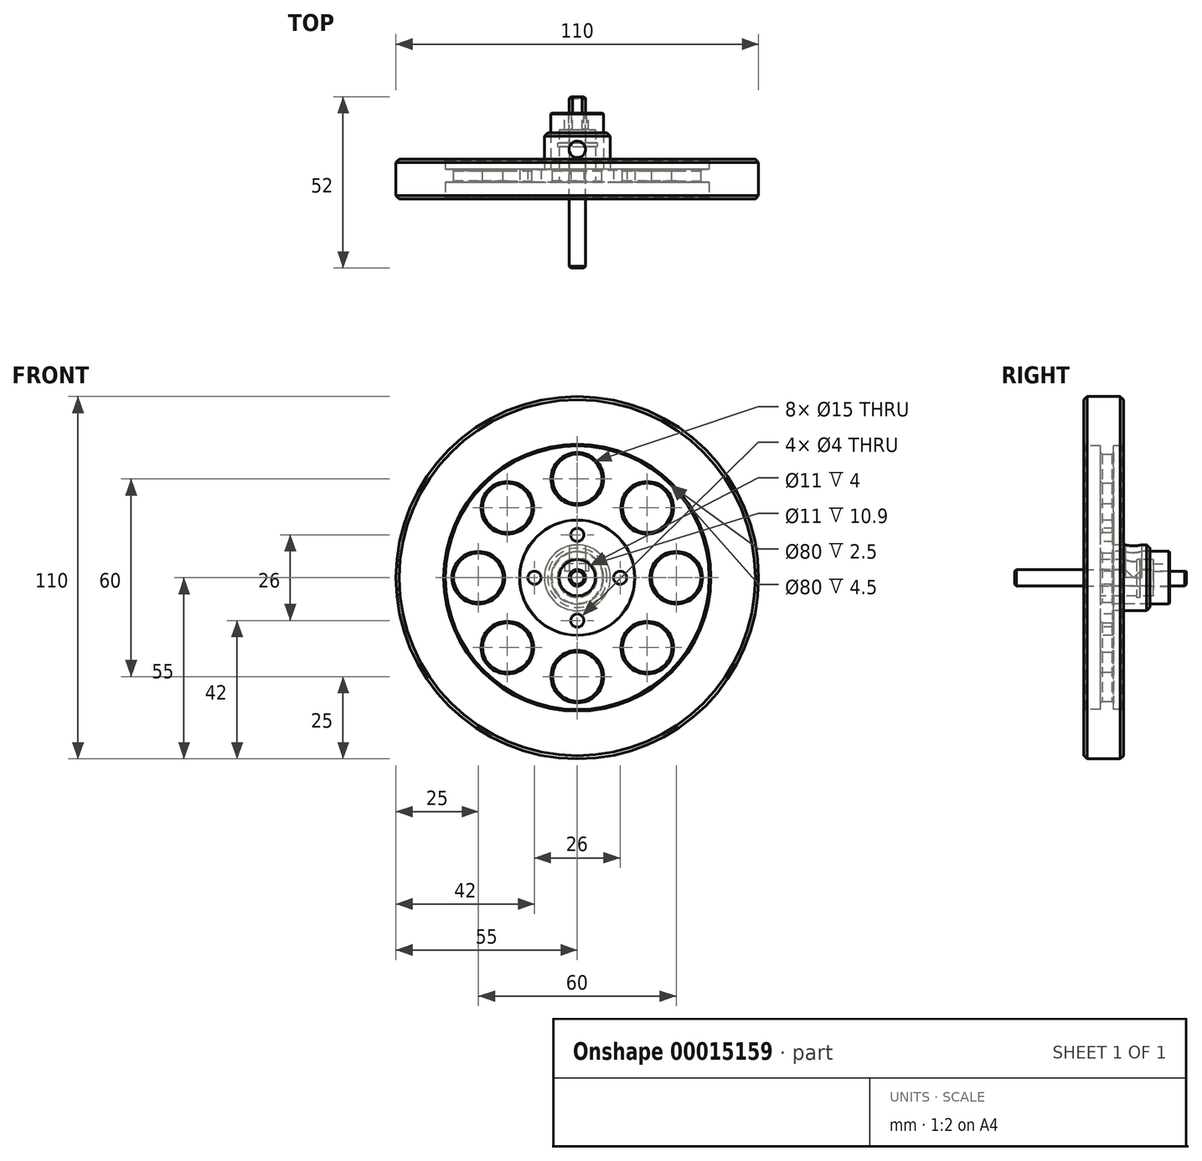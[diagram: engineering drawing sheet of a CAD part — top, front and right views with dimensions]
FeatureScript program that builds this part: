
annotation { "Feature Type Name" : "Feature", "Feature Type Description" : "" }
export const myFeature = defineFeature(function(context is Context, id is Id, definition is map)
    precondition{}
    {
        {
            var Q0;
            Q0=qCreatedBy(makeId("Right.planeOp"),FACE);
            var sketch = newSketch(context, id + "F0", { "sketchPlane" : qUnion([Q0])});
            skLineSegment(sketch, "E0", {"start": v(0, 5.5) * mm, "end": v(0, 17.5) * mm});
            skLineSegment(sketch, "E1", {"start": v(0, 17.5) * mm, "end": v(4, 17.5) * mm});
            skLineSegment(sketch, "E2", {"start": v(4, 17.5) * mm, "end": v(4, 8) * mm});
            skLineSegment(sketch, "E3", {"start": v(4, 8) * mm, "end": v(21, 8) * mm});
            skLineSegment(sketch, "E4", {"start": v(21, 8) * mm, "end": v(21, 2.75) * mm});
            skLineSegment(sketch, "E5", {"start": v(16, 2.75) * mm, "end": v(16, 5.5) * mm});
            skLineSegment(sketch, "E6", {"start": v(12, 5.5) * mm, "end": v(12, 6) * mm});
            skLineSegment(sketch, "E7", {"start": v(12, 6) * mm, "end": v(10.9, 6) * mm});
            skLineSegment(sketch, "E8", {"start": v(10.9, 6) * mm, "end": v(10.9, 5.5) * mm});
            skLineSegment(sketch, "E9", {"start": v(10.9, 5.5) * mm, "end": v(0, 5.5) * mm});
            skLineSegment(sketch, "E10", {"start": v(16, 2.75) * mm, "end": v(21, 2.75) * mm});
            skPoint(sketch, "E11.end.orphan", {"position": v(16, 0) * mm});
            skPoint(sketch, "E11.start.orphan", {"position": v(21, 0) * mm});
            skLineSegment(sketch, "E12", {"start": v(0, 0) * mm, "end": v(21, 0) * mm, "construction": true});
            skLineSegment(sketch, "E13", {"start": v(12, 5.5) * mm, "end": v(16, 5.5) * mm});
            skSolve(sketch);
        }
        {
            var Q0;
            Q0=makeQuery(id+"F0.imprint","IMPRINT",FACE,{"disambiguationData":[TD([[makeQuery(id+"F0.imprint","IMPRINT",EDGE,{"derivedFrom":sQuery(id+"F0.wireOp",EDGE,"E0")}),-1.0]])]});
            var Q1;
            Q1=sQuery(id+"F0.wireOp",EDGE,"E12");
            revolve(context, id + "F1", {"entities" : qUnion([Q0]), "axis" : qUnion([Q1]), "revolveType" : RevolveType.FULL});
        }
        {
            var Q0;
            Q0=makeQuery(id+"F1.opRevolve","SWEPT_FACE",FACE,{"disambiguationData":[OSD([sQuery(id+"F0.wireOp",EDGE,"E0")])]});
            var sketch = newSketch(context, id + "F2", { "sketchPlane" : qUnion([Q0])});
            skCircle(sketch, "E14", {"center": v(0, 0) * mm, "radius": 13 * mm, "construction": true});
            skLineSegment(sketch, "E15", {"start": v(0, 0) * mm, "end": v(-17.5, 0) * mm, "construction": true});
            skCircle(sketch, "E16", {"center": v(-13, 0) * mm, "radius": 2 * mm});
            skCircle(sketch, "E17.1.0", {"center": v(0, -13) * mm, "radius": 2 * mm});
            skCircle(sketch, "E17.2.0", {"center": v(13, 0) * mm, "radius": 2 * mm});
            skCircle(sketch, "E17.3.0", {"center": v(0, 13) * mm, "radius": 2 * mm});
            skSolve(sketch);
        }
        {
            var Q0;
            Q0=makeQuery(id+"F2.imprint","IMPRINT",FACE,{"disambiguationData":[TD([[makeQuery(id+"F2.imprint","IMPRINT",EDGE,{"derivedFrom":sQuery(id+"F2.wireOp",EDGE,"E17.3.0")}),1.0]])]});
            var Q1;
            Q1=makeQuery(id+"F2.imprint","IMPRINT",FACE,{"disambiguationData":[TD([[makeQuery(id+"F2.imprint","IMPRINT",EDGE,{"derivedFrom":sQuery(id+"F2.wireOp",EDGE,"E16")}),1.0]])]});
            var Q2;
            Q2=makeQuery(id+"F2.imprint","IMPRINT",FACE,{"disambiguationData":[TD([[makeQuery(id+"F2.imprint","IMPRINT",EDGE,{"derivedFrom":sQuery(id+"F2.wireOp",EDGE,"E17.1.0")}),1.0]])]});
            var Q3;
            Q3=makeQuery(id+"F2.imprint","IMPRINT",FACE,{"disambiguationData":[TD([[makeQuery(id+"F2.imprint","IMPRINT",EDGE,{"derivedFrom":sQuery(id+"F2.wireOp",EDGE,"E17.2.0")}),1.0]])]});
            extrude(context, id + "F3", {"entities" : qUnion([Q0, Q1, Q2, Q3]), "operationType" : NewBodyOperationType.REMOVE, "endBound" : BoundingType.THROUGH_ALL, "oppositeDirection" : true, "depth" : 25 * mm});
        }
        {
            var Q0;
            Q0=makeQuery(id+"F1.opRevolve","SWEPT_EDGE",EDGE,{"disambiguationData":[OSD([sQuery(id+"F0.wireOp",EDGE,"E3"),sQuery(id+"F0.wireOp",EDGE,"E4")])]});
            var Q1;
            Q1=makeQuery(id+"F1.opRevolve","SWEPT_EDGE",EDGE,{"disambiguationData":[OSD([sQuery(id+"F0.wireOp",EDGE,"E1"),sQuery(id+"F0.wireOp",EDGE,"E2")])]});
            var Q2;
            Q2=makeQuery(id+"F3.boolean.opBoolean","COPY",EDGE,{"derivedFrom":makeQuery(id+"F3.opExtrude","CAP_EDGE",EDGE,{"disambiguationData":[OSD([sQuery(id+"F2.wireOp",EDGE,"E16")])],"isStart":true})});
            var Q3;
            Q3=makeQuery(id+"F3.boolean.opBoolean","COPY",EDGE,{"derivedFrom":makeQuery(id+"F3.opExtrude","CAP_EDGE",EDGE,{"disambiguationData":[OSD([sQuery(id+"F2.wireOp",EDGE,"E17.3.0")])],"isStart":true})});
            var Q4;
            Q4=makeQuery(id+"F3.boolean.opBoolean","COPY",EDGE,{"derivedFrom":makeQuery(id+"F3.opExtrude","CAP_EDGE",EDGE,{"disambiguationData":[OSD([sQuery(id+"F2.wireOp",EDGE,"E17.2.0")])],"isStart":true})});
            var Q5;
            Q5=makeQuery(id+"F3.boolean.opBoolean","COPY",EDGE,{"derivedFrom":makeQuery(id+"F3.opExtrude","CAP_EDGE",EDGE,{"disambiguationData":[OSD([sQuery(id+"F2.wireOp",EDGE,"E17.1.0")])],"isStart":true})});
            chamfer(context, id + "F4", {"entities" : qUnion([Q0, Q1, Q2, Q3, Q4, Q5]), "width" : .25 * mm, "tangentPropagation" : true});
        }
        {
            var Q0;
            Q0=qCreatedBy(makeId("Front.planeOp"),FACE);
            var sketch = newSketch(context, id + "F5", { "sketchPlane" : qUnion([Q0])});
            skPoint(sketch, "E18.0", {"position": v(0, 0) * mm});
            skCircle(sketch, "E19", {"center": v(0, 0) * mm, "radius": 2.5 * mm});
            skSolve(sketch);
        }
        {
            var Q0;
            Q0=makeQuery(id+"F5.imprint","IMPRINT",FACE,{"disambiguationData":[TD([[makeQuery(id+"F5.imprint","IMPRINT",EDGE,{"derivedFrom":sQuery(id+"F5.wireOp",EDGE,"E19")}),1.0]])]});
            extrude(context, id + "F6", {"entities" : qUnion([Q0]), "endBound" : BoundingType.SYMMETRIC, "depth" : 52 * mm});
        }
        {
            var Q0;
            Q0=makeQuery(id+"F6.opExtrude","CAP_FACE",FACE,{"disambiguationData":[OSD([sQuery(id+"F5.wireOp",EDGE,"E19")])],"isStart":true});
            var sketch = newSketch(context, id + "F7", { "sketchPlane" : qUnion([Q0])});
            skLineSegment(sketch, "E20.bottom", {"start": v(-3.4, 4.22) * mm, "end": v(3.87, 4.22) * mm});
            skLineSegment(sketch, "E20.top", {"start": v(-3.4, 2) * mm, "end": v(3.87, 2) * mm});
            skLineSegment(sketch, "E20.left", {"start": v(-3.4, 4.22) * mm, "end": v(-3.4, 2) * mm});
            skLineSegment(sketch, "E20.right", {"start": v(3.87, 4.22) * mm, "end": v(3.87, 2) * mm});
            skSolve(sketch);
        }
        {
            var Q0;
            {var subQ0=makeQuery(id+"F6.opExtrude","CAP_EDGE",EDGE,{"disambiguationData":[OSD([sQuery(id+"F5.wireOp",EDGE,"E19")])],"isStart":true});var subQ1=sQuery(id+"F7.wireOp",EDGE,"E20.top");var subQ3=makeQuery(id+"F7.imprint","INTERSECT",VERTEX,{"disambiguationData":[OD(0.0)],"derivedFrom":[subQ0,subQ1]});Q0=makeQuery(id+"F7.imprint","IMPRINT",FACE,{"disambiguationData":[TD([[makeQuery(id+"F7.imprint","IMPRINT",EDGE,{"disambiguationData":[TD([[subQ3,-1.0]])],"derivedFrom":subQ1}),1.0]])]});}
            var Q1;
            Q1=makeQuery(id+"F7.imprint","IMPRINT",FACE,{"disambiguationData":[TD([[makeQuery(id+"F7.imprint","IMPRINT",EDGE,{"derivedFrom":sQuery(id+"F7.wireOp",EDGE,"E20.bottom")}),-1.0]])]});
            extrude(context, id + "F8", {"entities" : qUnion([Q0, Q1]), "operationType" : NewBodyOperationType.REMOVE, "oppositeDirection" : true, "depth" : 10 * mm});
        }
        {
            var Q0;
            Q0=makeQuery(id+"F6.opExtrude","CAP_EDGE",EDGE,{"disambiguationData":[OSD([sQuery(id+"F5.wireOp",EDGE,"E19")])],"isStart":false});
            var Q1;
            Q1=makeQuery(id+"F6.opExtrude","CAP_EDGE",EDGE,{"disambiguationData":[OSD([sQuery(id+"F5.wireOp",EDGE,"E19")])],"isStart":true});
            chamfer(context, id + "F9", {"entities" : qUnion([Q0, Q1]), "width" : .5 * mm, "tangentPropagation" : true});
        }
        {
            var Q0;
            Q0=qCreatedBy(makeId("Right.planeOp"),FACE);
            var sketch = newSketch(context, id + "F10", { "sketchPlane" : qUnion([Q0])});
            skLineSegment(sketch, "E21", {"start": v(0, 0) * mm, "end": v(23.32, 0) * mm, "construction": true});
            skLineSegment(sketch, "E22", {"start": v(0, 2.5) * mm, "end": v(0, 40) * mm});
            skLineSegment(sketch, "E23", {"start": v(0, 40) * mm, "end": v(-5, 40) * mm});
            skLineSegment(sketch, "E24", {"start": v(-5, 40) * mm, "end": v(-5, 55) * mm});
            skLineSegment(sketch, "E25", {"start": v(-5, 55) * mm, "end": v(7, 55) * mm});
            skLineSegment(sketch, "E26", {"start": v(7, 55) * mm, "end": v(7, 40) * mm});
            skLineSegment(sketch, "E27", {"start": v(7, 40) * mm, "end": v(4, 40) * mm});
            skLineSegment(sketch, "E28", {"start": v(4, 40) * mm, "end": v(4, 10) * mm});
            skLineSegment(sketch, "E29", {"start": v(4, 10) * mm, "end": v(15, 10) * mm});
            skLineSegment(sketch, "E30", {"start": v(15, 10) * mm, "end": v(15, 2.5) * mm});
            skLineSegment(sketch, "E31", {"start": v(15, 2.5) * mm, "end": v(0, 2.5) * mm});
            skLineSegment(sketch, "E32", {"start": v(0, 40) * mm, "end": v(4, 40) * mm, "construction": true});
            skSolve(sketch);
        }
        {
            var Q0;
            Q0=makeQuery(id+"F10.imprint","IMPRINT",FACE,{"disambiguationData":[TD([[makeQuery(id+"F10.imprint","IMPRINT",EDGE,{"derivedFrom":sQuery(id+"F10.wireOp",EDGE,"E22")}),-1.0]])]});
            var Q1;
            Q1=sQuery(id+"F10.wireOp",EDGE,"E21");
            revolve(context, id + "F11", {"entities" : qUnion([Q0]), "axis" : qUnion([Q1]), "revolveType" : RevolveType.FULL});
        }
        {
            var Q0;
            Q0=qCreatedBy(makeId("Top.planeOp"),FACE);
            var sketch = newSketch(context, id + "F12", { "sketchPlane" : qUnion([Q0])});
            skCircle(sketch, "E33", {"center": v(0, 10) * mm, "radius": 2.5 * mm});
            skLineSegment(sketch, "E34.0", {"start": v(10, 15) * mm, "end": v(-10, 15) * mm});
            skSolve(sketch);
        }
        {
            var Q0;
            Q0=makeQuery(id+"F12.imprint","IMPRINT",FACE,{"disambiguationData":[TD([[makeQuery(id+"F12.imprint","IMPRINT",EDGE,{"derivedFrom":sQuery(id+"F12.wireOp",EDGE,"E33")}),1.0]])]});
            extrude(context, id + "F13", {"entities" : qUnion([Q0]), "operationType" : NewBodyOperationType.REMOVE, "endBound" : BoundingType.THROUGH_ALL, "depth" : 25 * mm});
        }
        {
            var Q0;
            Q0=makeQuery(id+"F11.opRevolve","SWEPT_FACE",FACE,{"disambiguationData":[OSD([sQuery(id+"F10.wireOp",EDGE,"E28")])]});
            var sketch = newSketch(context, id + "F14", { "sketchPlane" : qUnion([Q0])});
            skCircle(sketch, "E35", {"center": v(0, 0) * mm, "radius": 30 * mm, "construction": true});
            skLineSegment(sketch, "E36", {"start": v(0, 0) * mm, "end": v(0, 73.34) * mm, "construction": true});
            skCircle(sketch, "E37", {"center": v(0, 30) * mm, "radius": 7.5 * mm});
            skCircle(sketch, "E38.1.0", {"center": v(-21.21, 21.21) * mm, "radius": 7.5 * mm});
            skCircle(sketch, "E38.2.0", {"center": v(-30, 0) * mm, "radius": 7.5 * mm});
            skCircle(sketch, "E38.3.0", {"center": v(-21.21, -21.21) * mm, "radius": 7.5 * mm});
            skCircle(sketch, "E38.4.0", {"center": v(0, -30) * mm, "radius": 7.5 * mm});
            skCircle(sketch, "E38.5.0", {"center": v(21.21, -21.21) * mm, "radius": 7.5 * mm});
            skCircle(sketch, "E38.6.0", {"center": v(30, 0) * mm, "radius": 7.5 * mm});
            skCircle(sketch, "E38.7.0", {"center": v(21.21, 21.21) * mm, "radius": 7.5 * mm});
            skSolve(sketch);
        }
        {
            var Q0;
            Q0=makeQuery(id+"F14.imprint","IMPRINT",FACE,{"disambiguationData":[TD([[makeQuery(id+"F14.imprint","IMPRINT",EDGE,{"derivedFrom":sQuery(id+"F14.wireOp",EDGE,"E37")}),1.0]])]});
            var Q1;
            Q1=makeQuery(id+"F14.imprint","IMPRINT",FACE,{"disambiguationData":[TD([[makeQuery(id+"F14.imprint","IMPRINT",EDGE,{"derivedFrom":sQuery(id+"F14.wireOp",EDGE,"E38.1.0")}),1.0]])]});
            var Q2;
            Q2=makeQuery(id+"F14.imprint","IMPRINT",FACE,{"disambiguationData":[TD([[makeQuery(id+"F14.imprint","IMPRINT",EDGE,{"derivedFrom":sQuery(id+"F14.wireOp",EDGE,"E38.2.0")}),1.0]])]});
            var Q3;
            Q3=makeQuery(id+"F14.imprint","IMPRINT",FACE,{"disambiguationData":[TD([[makeQuery(id+"F14.imprint","IMPRINT",EDGE,{"derivedFrom":sQuery(id+"F14.wireOp",EDGE,"E38.3.0")}),1.0]])]});
            var Q4;
            Q4=makeQuery(id+"F14.imprint","IMPRINT",FACE,{"disambiguationData":[TD([[makeQuery(id+"F14.imprint","IMPRINT",EDGE,{"derivedFrom":sQuery(id+"F14.wireOp",EDGE,"E38.4.0")}),1.0]])]});
            var Q5;
            Q5=makeQuery(id+"F14.imprint","IMPRINT",FACE,{"disambiguationData":[TD([[makeQuery(id+"F14.imprint","IMPRINT",EDGE,{"derivedFrom":sQuery(id+"F14.wireOp",EDGE,"E38.5.0")}),1.0]])]});
            var Q6;
            Q6=makeQuery(id+"F14.imprint","IMPRINT",FACE,{"disambiguationData":[TD([[makeQuery(id+"F14.imprint","IMPRINT",EDGE,{"derivedFrom":sQuery(id+"F14.wireOp",EDGE,"E38.6.0")}),1.0]])]});
            var Q7;
            Q7=makeQuery(id+"F14.imprint","IMPRINT",FACE,{"disambiguationData":[TD([[makeQuery(id+"F14.imprint","IMPRINT",EDGE,{"derivedFrom":sQuery(id+"F14.wireOp",EDGE,"E38.7.0")}),1.0]])]});
            extrude(context, id + "F15", {"entities" : qUnion([Q0, Q1, Q2, Q3, Q4, Q5, Q6, Q7]), "operationType" : NewBodyOperationType.REMOVE, "endBound" : BoundingType.THROUGH_ALL, "oppositeDirection" : true, "depth" : 25 * mm});
        }
        {
            var Q0;
            Q0=makeQuery(id+"F11.opRevolve","SWEPT_EDGE",EDGE,{"disambiguationData":[OSD([sQuery(id+"F10.wireOp",EDGE,"E25"),sQuery(id+"F10.wireOp",EDGE,"E26")])]});
            var Q1;
            Q1=makeQuery(id+"F11.opRevolve","SWEPT_EDGE",EDGE,{"disambiguationData":[OSD([sQuery(id+"F10.wireOp",EDGE,"E24"),sQuery(id+"F10.wireOp",EDGE,"E25")])]});
            var Q2;
            Q2=makeQuery(id+"F11.opRevolve","SWEPT_EDGE",EDGE,{"disambiguationData":[OSD([sQuery(id+"F10.wireOp",EDGE,"E29"),sQuery(id+"F10.wireOp",EDGE,"E30")])]});
            chamfer(context, id + "F16", {"entities" : qUnion([Q0, Q1, Q2]), "width" : 1 * mm, "tangentPropagation" : true});
        }
        {
            var Q0;
            Q0=makeQuery(id+"F15.boolean.opBoolean","COPY",FACE,{"derivedFrom":makeQuery(id+"F15.opExtrude","SWEPT_FACE",FACE,{"disambiguationData":[OSD([sQuery(id+"F14.wireOp",EDGE,"E38.4.0")])]})});
            var Q1;
            Q1=makeQuery(id+"F15.boolean.opBoolean","COPY",FACE,{"derivedFrom":makeQuery(id+"F15.opExtrude","SWEPT_FACE",FACE,{"disambiguationData":[OSD([sQuery(id+"F14.wireOp",EDGE,"E38.5.0")])]})});
            var Q2;
            Q2=makeQuery(id+"F15.boolean.opBoolean","COPY",FACE,{"derivedFrom":makeQuery(id+"F15.opExtrude","SWEPT_FACE",FACE,{"disambiguationData":[OSD([sQuery(id+"F14.wireOp",EDGE,"E38.6.0")])]})});
            var Q3;
            Q3=makeQuery(id+"F15.boolean.opBoolean","COPY",FACE,{"derivedFrom":makeQuery(id+"F15.opExtrude","SWEPT_FACE",FACE,{"disambiguationData":[OSD([sQuery(id+"F14.wireOp",EDGE,"E38.7.0")])]})});
            var Q4;
            Q4=makeQuery(id+"F15.boolean.opBoolean","COPY",FACE,{"derivedFrom":makeQuery(id+"F15.opExtrude","SWEPT_FACE",FACE,{"disambiguationData":[OSD([sQuery(id+"F14.wireOp",EDGE,"E37")])]})});
            var Q5;
            Q5=makeQuery(id+"F15.boolean.opBoolean","COPY",FACE,{"derivedFrom":makeQuery(id+"F15.opExtrude","SWEPT_FACE",FACE,{"disambiguationData":[OSD([sQuery(id+"F14.wireOp",EDGE,"E38.1.0")])]})});
            var Q6;
            Q6=makeQuery(id+"F15.boolean.opBoolean","COPY",FACE,{"derivedFrom":makeQuery(id+"F15.opExtrude","SWEPT_FACE",FACE,{"disambiguationData":[OSD([sQuery(id+"F14.wireOp",EDGE,"E38.2.0")])]})});
            var Q7;
            Q7=makeQuery(id+"F15.boolean.opBoolean","COPY",FACE,{"derivedFrom":makeQuery(id+"F15.opExtrude","SWEPT_FACE",FACE,{"disambiguationData":[OSD([sQuery(id+"F14.wireOp",EDGE,"E38.3.0")])]})});
            chamfer(context, id + "F17", {"entities" : qUnion([Q0, Q1, Q2, Q3, Q4, Q5, Q6, Q7]), "width" : .5 * mm, "tangentPropagation" : true});
        }
        {
            var Q0;
            Q0=makeQuery(id+"F11.opRevolve","SWEPT_EDGE",EDGE,{"disambiguationData":[OSD([sQuery(id+"F10.wireOp",EDGE,"E23"),sQuery(id+"F10.wireOp",EDGE,"E24")])]});
            var Q1;
            Q1=makeQuery(id+"F11.opRevolve","SWEPT_EDGE",EDGE,{"disambiguationData":[OSD([sQuery(id+"F10.wireOp",EDGE,"E26"),sQuery(id+"F10.wireOp",EDGE,"E27")])]});
            chamfer(context, id + "F18", {"entities" : qUnion([Q0, Q1]), "width" : .5 * mm, "tangentPropagation" : true});
        }
    });
